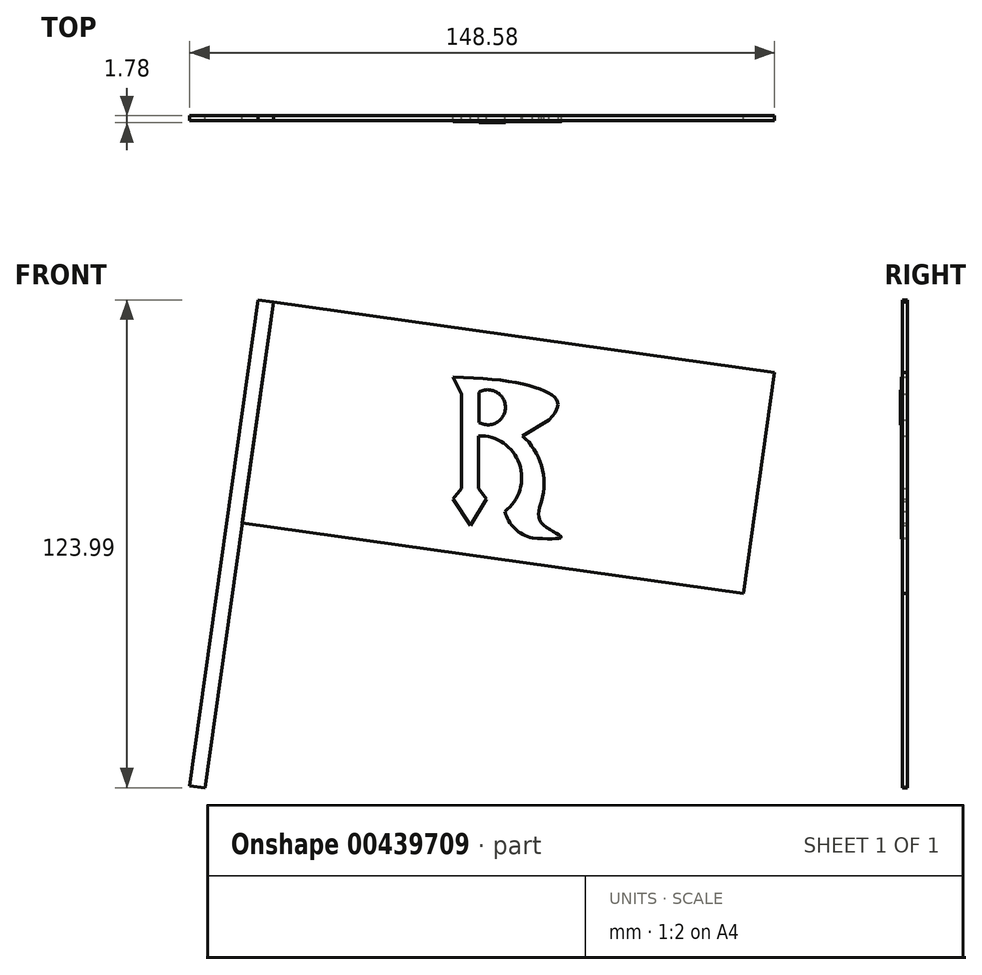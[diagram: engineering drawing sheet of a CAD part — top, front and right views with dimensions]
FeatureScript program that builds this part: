
annotation { "Feature Type Name" : "Feature", "Feature Type Description" : "" }
export const myFeature = defineFeature(function(context is Context, id is Id, definition is map)
    precondition{}
    {
        {
            var Q0;
            Q0=qCreatedBy(makeId("Front.planeOp"),FACE);
            var sketch = newSketch(context, id + "F0", { "sketchPlane" : qUnion([Q0])});
            skLineSegment(sketch, "E0", {"start": v(-64.23, -56.72) * mm, "end": v(-46.84, 66.73) * mm});
            skLineSegment(sketch, "E1", {"start": v(-46.84, 66.73) * mm, "end": v(-43, 66.18) * mm});
            skLineSegment(sketch, "E2", {"start": v(-43, 66.18) * mm, "end": v(-60.4, -57.26) * mm});
            skLineSegment(sketch, "E3", {"start": v(-60.4, -57.26) * mm, "end": v(-64.23, -56.72) * mm});
            skLineSegment(sketch, "E4", {"start": v(-43, 66.18) * mm, "end": v(84.35, 48.24) * mm});
            skLineSegment(sketch, "E5", {"start": v(84.35, 48.24) * mm, "end": v(76.44, -7.92) * mm});
            skLineSegment(sketch, "E6", {"start": v(76.44, -7.92) * mm, "end": v(-50.91, 10.03) * mm});
            skSolve(sketch);
        }
        {
            var Q0;
            {var subQ0=sQuery(id+"F0.wireOp",EDGE,"E4");Q0=makeQuery(id+"F0.imprint","IMPRINT",FACE,{"disambiguationData":[TD([[makeQuery(id+"F0.imprint","IMPRINT",EDGE,{"derivedFrom":subQ0}),-1.0]])]});}
            var sketch = newSketch(context, id + "F1", { "sketchPlane" : qUnion([Q0])});
            skLineSegment(sketch, "E7", {"start": v(2.61, 47.1) * mm, "end": v(4.83, 42.82) * mm});
            skLineSegment(sketch, "E8", {"start": v(4.83, 42.82) * mm, "end": v(4.83, 18.86) * mm});
            skLineSegment(sketch, "E9", {"start": v(4.83, 18.86) * mm, "end": v(2.61, 16.16) * mm});
            skLineSegment(sketch, "E10", {"start": v(2.61, 16.16) * mm, "end": v(7.05, 9.34) * mm});
            skLineSegment(sketch, "E11", {"start": v(7.05, 9.34) * mm, "end": v(11.18, 16.16) * mm});
            skLineSegment(sketch, "E12", {"start": v(11.18, 16.16) * mm, "end": v(9.12, 18.86) * mm});
            skLineSegment(sketch, "E13", {"start": v(9.12, 18.86) * mm, "end": v(9.12, 32.19) * mm});
            skLineSegment(sketch, "E14", {"start": v(27.05, 36.22) * mm, "end": v(20.23, 32.19) * mm});
            skArc(sketch, "E15", {"start": v(15.78, 12.99) * mm, "mid": v(19.5, 25.03) * mm, "end": v(9.12, 32.19) * mm});
            skArc(sketch, "E16", {"start": v(15.78, 12.99) * mm, "mid": v(18.35, 8.63) * mm, "end": v(22.76, 6.16) * mm});
            skArc(sketch, "E17", {"start": v(25.1, 15.53) * mm, "mid": v(25.14, 24.58) * mm, "end": v(20.23, 32.19) * mm});
            skFitSpline(sketch, "E18", {"points": [v(25.1, 15.53) * mm, v(25.1, 10.1) * mm, v(30.08, 6.5) * mm, v(22.76, 6.16) * mm], "startDerivative": vector(-6.1, -18.63) * mm, "endDerivative": vector(-31.27, 1.32) * mm});
            skFitSpline(sketch, "E19", {"points": [v(2.61, 47.1) * mm, v(28.8, 41.52) * mm, v(27.05, 36.22) * mm], "startDerivative": vector(62.08, -1.08) * mm, "endDerivative": vector(-21.7, -22.88) * mm});
            skSolve(sketch);
        }
        {
            var Q0;
            {var subQ0=sQuery(id+"F0.wireOp",EDGE,"E4");Q0=makeQuery(id+"F0.imprint","IMPRINT",FACE,{"disambiguationData":[TD([[makeQuery(id+"F0.imprint","IMPRINT",EDGE,{"derivedFrom":subQ0}),-1.0]])]});}
            var sketch = newSketch(context, id + "F2", { "sketchPlane" : qUnion([Q0])});
            skLineSegment(sketch, "E20", {"start": v(9.2, 43.23) * mm, "end": v(9.2, 35.6) * mm});
            skArc(sketch, "E21", {"start": v(9.2, 35.6) * mm, "mid": v(15.95, 39.42) * mm, "end": v(9.2, 43.23) * mm});
            skSolve(sketch);
        }
        {
            var Q0;
            Q0=makeQuery(id+"F0.imprint","IMPRINT",FACE,{"disambiguationData":[TD([[makeQuery(id+"F0.imprint","IMPRINT",EDGE,{"derivedFrom":sQuery(id+"F0.wireOp",EDGE,"E0")}),-1.0]])]});
            extrude(context, id + "F3", {"entities" : qUnion([Q0]), "depth" : 1.27 * mm});
        }
        {
            var Q0;
            Q0 = qSketchRegion(id + "F1", true);
            extrude(context, id + "F4", {"entities" : qUnion([Q0]), "operationType" : NewBodyOperationType.ADD, "depth" : 1.52 * mm});
        }
        {
            var Q0;
            Q0 = qSketchRegion(id + "F2", true);
            extrude(context, id + "F5", {"entities" : qUnion([Q0]), "operationType" : NewBodyOperationType.ADD, "depth" : 1.78 * mm});
        }
        {
            var Q0;
            {var subQ0=sQuery(id+"F0.wireOp",EDGE,"E4");Q0=makeQuery(id+"F0.imprint","IMPRINT",FACE,{"disambiguationData":[TD([[makeQuery(id+"F0.imprint","IMPRINT",EDGE,{"derivedFrom":subQ0}),-1.0]])]});}
            extrude(context, id + "F6", {"entities" : qUnion([Q0]), "depth" : 1.27 * mm});
        }
    });
